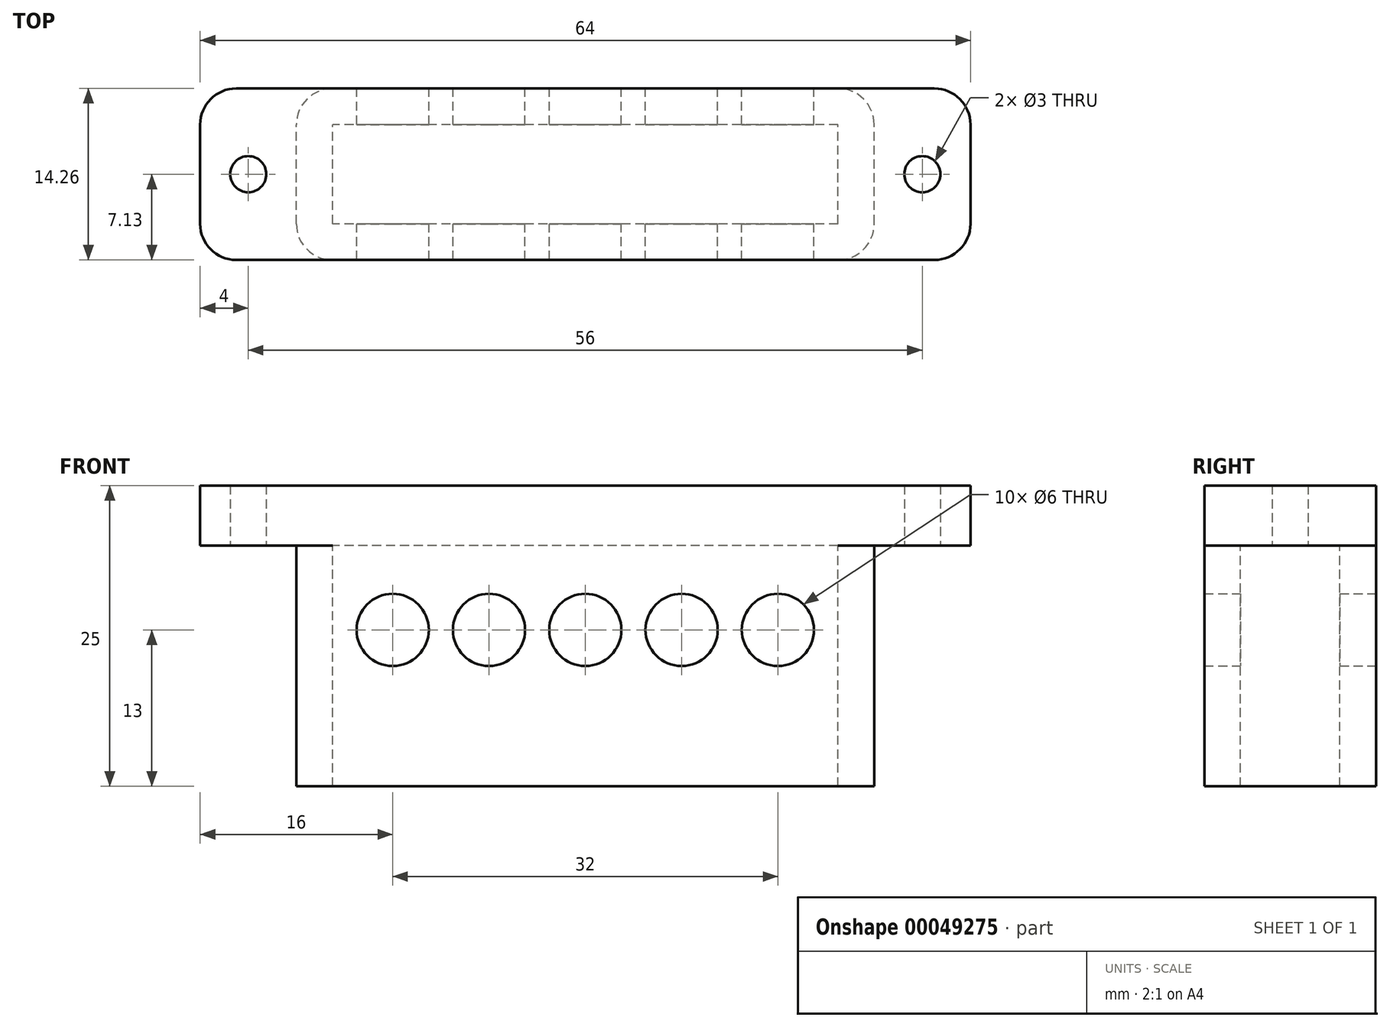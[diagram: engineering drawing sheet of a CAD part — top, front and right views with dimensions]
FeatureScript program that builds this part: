
annotation { "Feature Type Name" : "Feature", "Feature Type Description" : "" }
export const myFeature = defineFeature(function(context is Context, id is Id, definition is map)
    precondition{}
    {
        {
            var Q0;
            Q0=qCreatedBy(makeId("Top.planeOp"),FACE);
            var sketch = newSketch(context, id + "F0", { "sketchPlane" : qUnion([Q0])});
            skPoint(sketch, "E0.rect.middle", {"position": v(0, 0) * mm});
            skLineSegment(sketch, "E1.rect.bottom", {"start": v(21, -4.13) * mm, "end": v(-21, -4.12) * mm});
            skLineSegment(sketch, "E1.rect.top", {"start": v(21, 4.12) * mm, "end": v(-21, 4.13) * mm});
            skLineSegment(sketch, "E1.rect.left", {"start": v(21, -4.13) * mm, "end": v(21, 4.12) * mm});
            skLineSegment(sketch, "E1.rect.right", {"start": v(-21, -4.12) * mm, "end": v(-21, 4.13) * mm});
            skLineSegment(sketch, "E2.0", {"start": v(21, 7.12) * mm, "end": v(-21, 7.13) * mm});
            skLineSegment(sketch, "E2.1", {"start": v(24, -4.13) * mm, "end": v(24, 4.12) * mm});
            skLineSegment(sketch, "E2.2", {"start": v(21, -7.13) * mm, "end": v(-21, -7.12) * mm});
            skLineSegment(sketch, "E2.3", {"start": v(-24, -4.12) * mm, "end": v(-24, 4.13) * mm});
            skLineSegment(sketch, "E3", {"start": v(0, -17.3) * mm, "end": v(0, 15.57) * mm, "construction": true});
            skPoint(sketch, "E4.visualSharp", {"position": v(-24, 7.13) * mm});
            skArc(sketch, "E4.filletArc", {"start": v(-21, 7.13) * mm, "mid": v(-23.12, 6.25) * mm, "end": v(-24, 4.13) * mm});
            skPoint(sketch, "E5.visualSharp", {"position": v(24, 7.12) * mm});
            skArc(sketch, "E5.filletArc", {"start": v(24, 4.12) * mm, "mid": v(23.12, 6.25) * mm, "end": v(21, 7.12) * mm});
            skPoint(sketch, "E6.visualSharp", {"position": v(24, -7.13) * mm});
            skArc(sketch, "E6.filletArc", {"start": v(21, -7.13) * mm, "mid": v(23.12, -6.25) * mm, "end": v(24, -4.13) * mm});
            skPoint(sketch, "E7.visualSharp", {"position": v(-24, -7.12) * mm});
            skArc(sketch, "E7.filletArc", {"start": v(-24, -4.12) * mm, "mid": v(-23.12, -6.25) * mm, "end": v(-21, -7.12) * mm});
            skLineSegment(sketch, "E8", {"start": v(-21, 7.13) * mm, "end": v(-29, 7.13) * mm});
            skLineSegment(sketch, "E9", {"start": v(-32, 4.13) * mm, "end": v(-32, -4.12) * mm});
            skLineSegment(sketch, "E10", {"start": v(-29, -7.12) * mm, "end": v(-21, -7.12) * mm});
            skLineSegment(sketch, "E11.MirrorCS", {"start": v(21, 7.12) * mm, "end": v(29, 7.12) * mm});
            skLineSegment(sketch, "E12.MirrorCS", {"start": v(32, 4.13) * mm, "end": v(32, -4.12) * mm});
            skLineSegment(sketch, "E13.MirrorCS", {"start": v(29, -7.12) * mm, "end": v(21, -7.12) * mm});
            skPoint(sketch, "E14.visualSharp", {"position": v(-32, 7.13) * mm});
            skArc(sketch, "E14.filletArc", {"start": v(-29, 7.13) * mm, "mid": v(-31.12, 6.25) * mm, "end": v(-32, 4.13) * mm});
            skPoint(sketch, "E15.visualSharp", {"position": v(-32, -7.12) * mm});
            skArc(sketch, "E15.filletArc", {"start": v(-32, -4.12) * mm, "mid": v(-31.12, -6.25) * mm, "end": v(-29, -7.12) * mm});
            skPoint(sketch, "E16.visualSharp", {"position": v(32, 7.13) * mm});
            skArc(sketch, "E16.filletArc", {"start": v(32, 4.13) * mm, "mid": v(31.12, 6.25) * mm, "end": v(29, 7.13) * mm});
            skPoint(sketch, "E17.visualSharp", {"position": v(32, -7.12) * mm});
            skArc(sketch, "E17.filletArc", {"start": v(29, -7.12) * mm, "mid": v(31.12, -6.25) * mm, "end": v(32, -4.12) * mm});
            skLineSegment(sketch, "E18", {"start": v(32, 4.13) * mm, "end": v(24, -4.13) * mm, "construction": true});
            skPoint(sketch, "E19", {"position": v(28, 0) * mm});
            skPoint(sketch, "E20.MirrorP", {"position": v(-28, 0) * mm});
            skSolve(sketch);
        }
        {
            var Q0;
            Q0=makeQuery(id+"F0.imprint","IMPRINT",FACE,{"disambiguationData":[TD([[makeQuery(id+"F0.imprint","IMPRINT",EDGE,{"derivedFrom":sQuery(id+"F0.wireOp",EDGE,"E2.3")}),1.0]])]});
            var Q1;
            Q1=makeQuery(id+"F0.imprint","IMPRINT",FACE,{"disambiguationData":[TD([[makeQuery(id+"F0.imprint","IMPRINT",EDGE,{"derivedFrom":sQuery(id+"F0.wireOp",EDGE,"E1.rect.bottom")}),1.0]])]});
            var Q2;
            Q2=makeQuery(id+"F0.imprint","IMPRINT",FACE,{"disambiguationData":[TD([[makeQuery(id+"F0.imprint","IMPRINT",EDGE,{"derivedFrom":sQuery(id+"F0.wireOp",EDGE,"E2.1")}),-1.0]])]});
            var Q3;
            Q3=makeQuery(id+"F0.imprint","IMPRINT",FACE,{"disambiguationData":[TD([[makeQuery(id+"F0.imprint","IMPRINT",EDGE,{"derivedFrom":sQuery(id+"F0.wireOp",EDGE,"E1.rect.bottom")}),-1.0]])]});
            extrude(context, id + "F1", {"entities" : qUnion([Q0, Q1, Q2, Q3]), "depth" : 5 * mm});
        }
        {
            var Q0;
            Q0=makeQuery(id+"F0.imprint","IMPRINT",FACE,{"disambiguationData":[TD([[makeQuery(id+"F0.imprint","IMPRINT",EDGE,{"derivedFrom":sQuery(id+"F0.wireOp",EDGE,"E1.rect.bottom")}),1.0]])]});
            extrude(context, id + "F2", {"entities" : qUnion([Q0]), "operationType" : NewBodyOperationType.ADD, "oppositeDirection" : true, "depth" : 20 * mm});
        }
        {
            var Q0;
            {var subQ0=sQuery(id+"F0.wireOp",EDGE,"E2.0");Q0=makeQuery(id+"F2.boolean.opBoolean","MERGE",FACE,{"derivedFrom":[makeQuery(id+"F1.opExtrude","SWEPT_FACE",FACE,{"disambiguationData":[OSD([subQ0,sQuery(id+"F0.wireOp",EDGE,"E8"),sQuery(id+"F0.wireOp",EDGE,"E11.MirrorCS")])]}),makeQuery(id+"F2.opExtrude","SWEPT_FACE",FACE,{"disambiguationData":[OSD([subQ0])]})]});}
            var sketch = newSketch(context, id + "F3", { "sketchPlane" : qUnion([Q0])});
            skLineSegment(sketch, "E21.0", {"start": v(21, -20) * mm, "end": v(21, 0) * mm});
            skLineSegment(sketch, "E21.1", {"start": v(-21, -20) * mm, "end": v(-21, 0) * mm});
            skLineSegment(sketch, "E22", {"start": v(-28.2, -4) * mm, "end": v(30.76, -4) * mm, "construction": true});
            skCircle(sketch, "E23", {"center": v(16, -7) * mm, "radius": 3 * mm});
            skCircle(sketch, "E24.1.0.0", {"center": v(8, -7) * mm, "radius": 3 * mm});
            skCircle(sketch, "E24.2.0.0", {"center": v(0, -7) * mm, "radius": 3 * mm});
            skCircle(sketch, "E24.3.0.0", {"center": v(-8, -7) * mm, "radius": 3 * mm});
            skCircle(sketch, "E24.4.0.0", {"center": v(-16, -7) * mm, "radius": 3 * mm});
            skLineSegment(sketch, "E24.direction1", {"start": v(16, -7) * mm, "end": v(8, -7) * mm, "construction": true});
            skLineSegment(sketch, "E25", {"start": v(0, 16.02) * mm, "end": v(0, -26.78) * mm, "construction": true});
            skSolve(sketch);
        }
        {
            var Q0;
            Q0=makeQuery(id+"F3.imprint","IMPRINT",FACE,{"disambiguationData":[TD([[makeQuery(id+"F3.imprint","IMPRINT",EDGE,{"derivedFrom":sQuery(id+"F3.wireOp",EDGE,"E24.4.0.0")}),1.0]])]});
            var Q1;
            Q1=makeQuery(id+"F3.imprint","IMPRINT",FACE,{"disambiguationData":[TD([[makeQuery(id+"F3.imprint","IMPRINT",EDGE,{"derivedFrom":sQuery(id+"F3.wireOp",EDGE,"E24.3.0.0")}),1.0]])]});
            var Q2;
            Q2=makeQuery(id+"F3.imprint","IMPRINT",FACE,{"disambiguationData":[TD([[makeQuery(id+"F3.imprint","IMPRINT",EDGE,{"derivedFrom":sQuery(id+"F3.wireOp",EDGE,"E24.2.0.0")}),1.0]])]});
            var Q3;
            Q3=makeQuery(id+"F3.imprint","IMPRINT",FACE,{"disambiguationData":[TD([[makeQuery(id+"F3.imprint","IMPRINT",EDGE,{"derivedFrom":sQuery(id+"F3.wireOp",EDGE,"E24.1.0.0")}),1.0]])]});
            var Q4;
            Q4=makeQuery(id+"F3.imprint","IMPRINT",FACE,{"disambiguationData":[TD([[makeQuery(id+"F3.imprint","IMPRINT",EDGE,{"derivedFrom":sQuery(id+"F3.wireOp",EDGE,"E23")}),1.0]])]});
            extrude(context, id + "F4", {"entities" : qUnion([Q0, Q1, Q2, Q3, Q4]), "operationType" : NewBodyOperationType.REMOVE, "oppositeDirection" : true, "depth" : 25 * mm});
        }
        {
            var Q0;
            Q0=sQuery(id+"F0.wireOp",VERTEX,"E19");
            var Q1;
            Q1=sQuery(id+"F0.wireOp",VERTEX,"E20.MirrorP");
            var Q2;
            Q2=makeQuery(id+"F1.opExtrude","SWEPT_BODY",BODY,{"disambiguationData":[OSD([sQuery(id+"F0.wireOp",EDGE,"E2.0"),sQuery(id+"F0.wireOp",EDGE,"E2.2"),sQuery(id+"F0.wireOp",EDGE,"E8"),sQuery(id+"F0.wireOp",EDGE,"E9"),sQuery(id+"F0.wireOp",EDGE,"E10"),sQuery(id+"F0.wireOp",EDGE,"E11.MirrorCS"),sQuery(id+"F0.wireOp",EDGE,"E12.MirrorCS"),sQuery(id+"F0.wireOp",EDGE,"E13.MirrorCS"),sQuery(id+"F0.wireOp",EDGE,"E14.filletArc"),sQuery(id+"F0.wireOp",EDGE,"E15.filletArc"),sQuery(id+"F0.wireOp",EDGE,"E16.filletArc"),sQuery(id+"F0.wireOp",EDGE,"E17.filletArc")])]});
            hole(context, id + "F5", {"style" : HoleStyle.SIMPLE, "holeDiameter" : 3 * mm, "endStyle" : HoleEndStyle.THROUGH, "oppositeDirection" : true, "locations" : qUnion([Q0, Q1]), "scope" : qUnion([Q2])});
        }
    });
